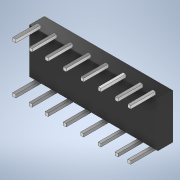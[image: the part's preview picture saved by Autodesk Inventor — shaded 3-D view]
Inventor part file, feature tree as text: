
AUTODESK INVENTOR PART (.ipt)
format: ipt  version: 2021 (Build 250183000, 183)  size: 289,280 bytes
history: native  units: mm
features: sketch x4, extrude x3
ambient origin geometry x8: Origin, YZ Plane, XZ Plane, XY Plane, X Axis, Y Axis, Z Axis, Center Point
bodies: Solid1 (feature_tree)
feature tree (7):
  extrude  "Extrusion1"  Depth=15.0mm
  sketch  "Sketch2"  dims[d2=5.0mm d3=0.0mm d4=1.0mm d5=0.0mm]
  extrude  "Extrusion2"  Depth=1.0mm TaperAngle=0.0deg
  extrude  "Extrusion3"  [1 undecoded]
  sketch  "Sketch1"  dims[d0=43.0mm d1=15.0mm]
  sketch  "Sketch3"  dims[d6=1.0mm d7=0.0mm]
  sketch  "Sketch4"
note: 1 required parameter value undecoded (feature->parameter linkage not recoverable at this tier; creation-order binding heuristic only, values carry confidence <= 0.55)
